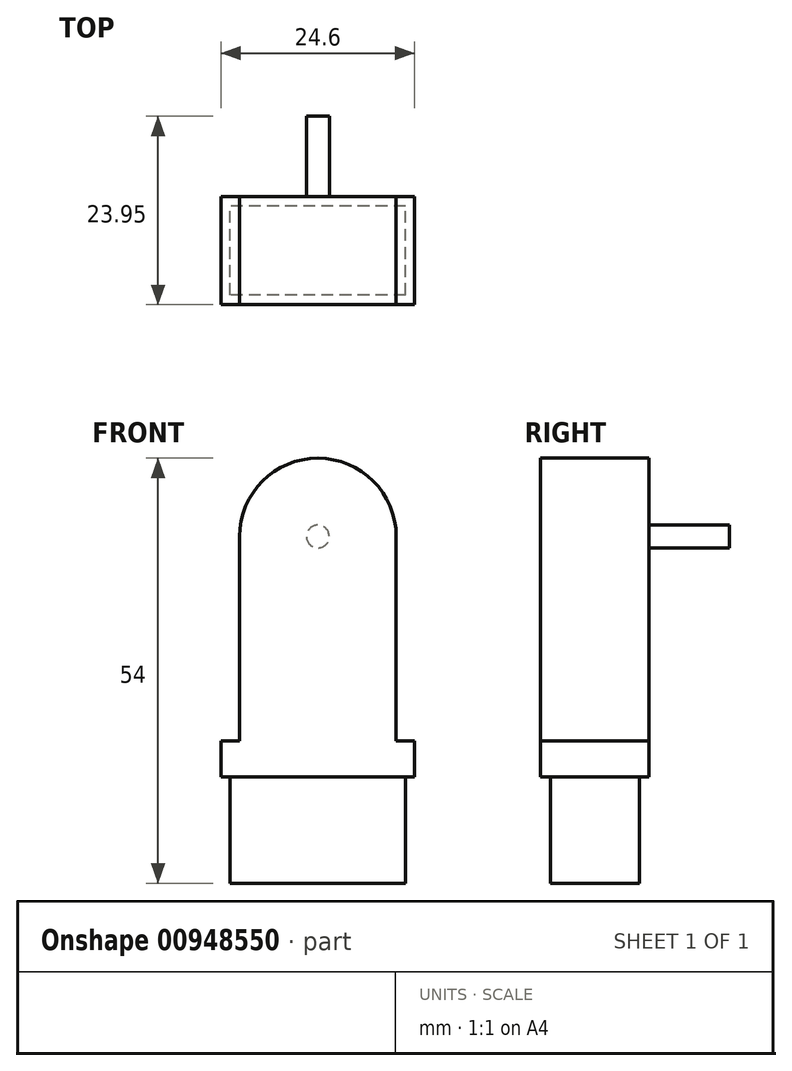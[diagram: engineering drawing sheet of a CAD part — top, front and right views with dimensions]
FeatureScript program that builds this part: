
annotation { "Feature Type Name" : "Feature", "Feature Type Description" : "" }
export const myFeature = defineFeature(function(context is Context, id is Id, definition is map)
    precondition{}
    {
        {
            var Q0;
            Q0=qCreatedBy(makeId("Front.planeOp"),FACE);
            var sketch = newSketch(context, id + "F0", { "sketchPlane" : qUnion([Q0])});
            skLineSegment(sketch, "E0.bottom", {"start": v(-9.95, 0) * mm, "end": v(9.95, 0) * mm});
            skLineSegment(sketch, "E0.top", {"start": v(-9.95, -30.55) * mm, "end": v(9.95, -30.55) * mm});
            skLineSegment(sketch, "E0.left", {"start": v(-9.95, 0) * mm, "end": v(-9.95, -30.55) * mm});
            skLineSegment(sketch, "E0.right", {"start": v(9.95, 0) * mm, "end": v(9.95, -30.55) * mm});
            skArc(sketch, "E1", {"start": v(-9.95, 0) * mm, "mid": v(0, 9.95) * mm, "end": v(9.95, 0) * mm});
            skSolve(sketch);
        }
        {
            var Q0;
            Q0 = qSketchRegion(id + "F0", true);
            extrude(context, id + "F1", {"entities" : qUnion([Q0]), "depth" : 13.75 * mm, "offsetDistance" : 25 * mm});
        }
        {
            var Q0;
            Q0=makeQuery(id+"F1.opExtrude","CAP_FACE",FACE,{"disambiguationData":[OSD([sQuery(id+"F0.wireOp",EDGE,"E0.top"),sQuery(id+"F0.wireOp",EDGE,"E0.left"),sQuery(id+"F0.wireOp",EDGE,"E0.right"),sQuery(id+"F0.wireOp",EDGE,"E1")])],"isStart":true});
            var sketch = newSketch(context, id + "F2", { "sketchPlane" : qUnion([Q0])});
            skCircle(sketch, "E2", {"center": v(0, 0) * mm, "radius": 1.45 * mm});
            skLineSegment(sketch, "E3", {"start": v(-1.1, -0.95) * mm, "end": v(1.1, -0.95) * mm});
            skSolve(sketch);
        }
        {
            var Q0;
            Q0 = qSketchRegion(id + "F2", true);
            extrude(context, id + "F3", {"entities" : qUnion([Q0]), "operationType" : NewBodyOperationType.ADD, "depth" : 10.2 * mm, "offsetDistance" : 25 * mm});
        }
        {
            var Q0;
            Q0=makeQuery(id+"F1.opExtrude","SWEPT_FACE",FACE,{"disambiguationData":[OSD([sQuery(id+"F0.wireOp",EDGE,"E0.top")])]});
            cPlane(context, id + "F4", {"entities" : qUnion([Q0]), "cplaneType" : CPlaneType.OFFSET, "offset" : 0 * mm, "width" : 150 * mm, "height" : 150 * mm});
        }
        {
            var Q0;
            Q0=qCreatedBy(id+"F4.planeOp",FACE);
            var sketch = newSketch(context, id + "F5", { "sketchPlane" : qUnion([Q0])});
            skLineSegment(sketch, "E4.bottom", {"start": v(-9.95, 0) * mm, "end": v(9.95, 0) * mm, "construction": true});
            skLineSegment(sketch, "E4.top", {"start": v(-9.95, 13.75) * mm, "end": v(9.95, 13.75) * mm, "construction": true});
            skLineSegment(sketch, "E4.left", {"start": v(-9.95, 0) * mm, "end": v(-9.95, 13.75) * mm, "construction": true});
            skLineSegment(sketch, "E4.right", {"start": v(9.95, 0) * mm, "end": v(9.95, 13.75) * mm, "construction": true});
            skPoint(sketch, "E4.middle", {"position": v(0, 6.88) * mm});
            skLineSegment(sketch, "E5.bottom", {"start": v(-12.3, 0) * mm, "end": v(12.3, 0) * mm});
            skLineSegment(sketch, "E5.top", {"start": v(-12.3, 13.75) * mm, "end": v(12.3, 13.75) * mm});
            skLineSegment(sketch, "E5.left", {"start": v(-12.3, 0) * mm, "end": v(-12.3, 13.75) * mm});
            skLineSegment(sketch, "E5.right", {"start": v(12.3, 0) * mm, "end": v(12.3, 13.75) * mm});
            skSolve(sketch);
        }
        {
            var Q0;
            Q0=makeQuery(id+"F5.imprint","IMPRINT",FACE,{"disambiguationData":[TD([[makeQuery(id+"F5.imprint","IMPRINT",EDGE,{"derivedFrom":sQuery(id+"F5.wireOp",EDGE,"E5.bottom")}),1.0]])]});
            extrude(context, id + "F6", {"entities" : qUnion([Q0]), "operationType" : NewBodyOperationType.ADD, "oppositeDirection" : true, "depth" : 4.6 * mm, "offsetDistance" : 25 * mm});
        }
        {
            var Q0;
            Q0=qCreatedBy(id+"F4.planeOp",FACE);
            var sketch = newSketch(context, id + "F7", { "sketchPlane" : qUnion([Q0])});
            skLineSegment(sketch, "E6.bottom", {"start": v(11.15, 12.53) * mm, "end": v(-11.15, 12.53) * mm});
            skLineSegment(sketch, "E6.top", {"start": v(11.15, 1.23) * mm, "end": v(-11.15, 1.22) * mm});
            skLineSegment(sketch, "E6.left", {"start": v(11.15, 12.53) * mm, "end": v(11.15, 1.23) * mm});
            skLineSegment(sketch, "E6.right", {"start": v(-11.15, 12.53) * mm, "end": v(-11.15, 1.22) * mm});
            skPoint(sketch, "E6.middle", {"position": v(0, 6.88) * mm});
            skSolve(sketch);
        }
        {
            var Q0;
            Q0 = qSketchRegion(id + "F7", true);
            extrude(context, id + "F8", {"entities" : qUnion([Q0]), "operationType" : NewBodyOperationType.ADD, "depth" : 13.5 * mm, "offsetDistance" : 25 * mm});
        }
    });
